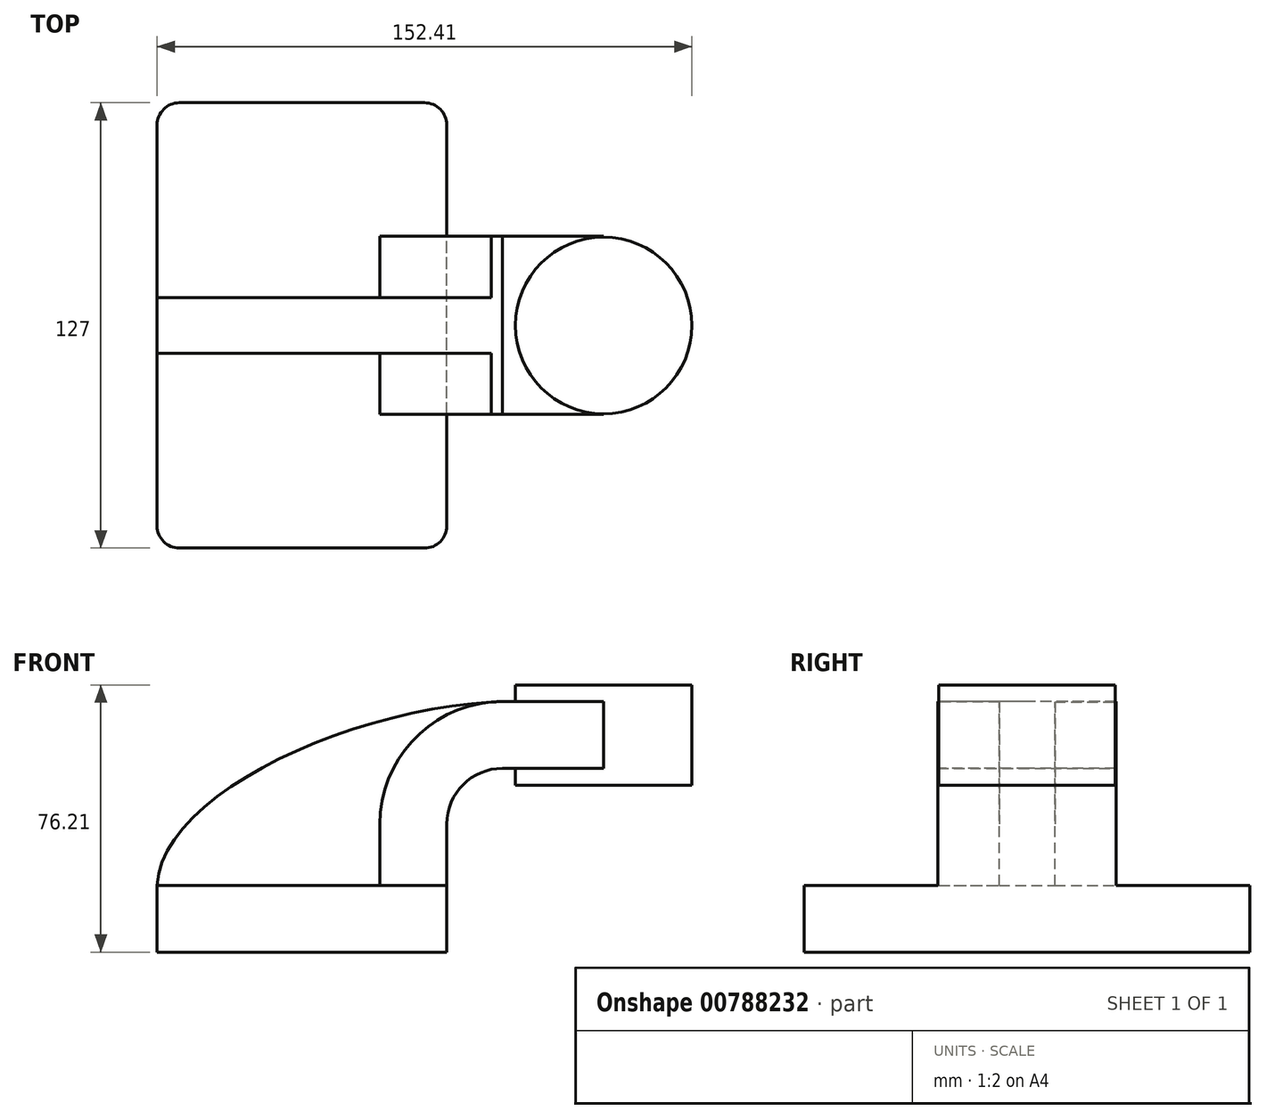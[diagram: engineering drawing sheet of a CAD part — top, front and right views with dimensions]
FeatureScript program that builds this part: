
annotation { "Feature Type Name" : "Feature", "Feature Type Description" : "" }
export const myFeature = defineFeature(function(context is Context, id is Id, definition is map)
    precondition{}
    {
        {
            var Q0;
            Q0=qCreatedBy(makeId("Front.planeOp"),FACE);
            var sketch = newSketch(context, id + "F0", { "sketchPlane" : qUnion([Q0])});
            skLineSegment(sketch, "E0.bottom", {"start": v(-41.27, -9.53) * mm, "end": v(41.28, -9.53) * mm});
            skLineSegment(sketch, "E0.top", {"start": v(-41.28, 9.53) * mm, "end": v(41.28, 9.53) * mm});
            skLineSegment(sketch, "E0.left", {"start": v(-41.28, -9.53) * mm, "end": v(-41.28, 9.53) * mm});
            skLineSegment(sketch, "E0.right", {"start": v(41.28, -9.53) * mm, "end": v(41.28, 9.53) * mm});
            skPoint(sketch, "E0.middle", {"position": v(0, 0) * mm});
            skLineSegment(sketch, "E1.bottom", {"start": v(60.32, 38.1) * mm, "end": v(111.12, 38.1) * mm});
            skLineSegment(sketch, "E1.top", {"start": v(60.32, 66.67) * mm, "end": v(111.12, 66.67) * mm});
            skLineSegment(sketch, "E1.left", {"start": v(60.32, 38.1) * mm, "end": v(60.32, 66.67) * mm});
            skLineSegment(sketch, "E1.right", {"start": v(111.12, 38.1) * mm, "end": v(111.12, 66.67) * mm});
            skPoint(sketch, "E1.middle", {"position": v(85.72, 52.39) * mm});
            skLineSegment(sketch, "E2", {"start": v(41.27, 9.53) * mm, "end": v(41.27, 27) * mm});
            skArc(sketch, "E3", {"start": v(41.27, 27) * mm, "mid": v(45.92, 38.23) * mm, "end": v(57.15, 42.88) * mm});
            skLineSegment(sketch, "E4", {"start": v(57.15, 42.88) * mm, "end": v(85.96, 42.88) * mm});
            skLineSegment(sketch, "E5.0", {"start": v(57.15, 61.93) * mm, "end": v(85.96, 61.93) * mm});
            skArc(sketch, "E5.1", {"start": v(22.23, 27) * mm, "mid": v(32.45, 51.7) * mm, "end": v(57.15, 61.93) * mm});
            skLineSegment(sketch, "E5.2", {"start": v(22.22, 9.53) * mm, "end": v(22.22, 27) * mm});
            skLineSegment(sketch, "E6", {"start": v(85.96, 38.1) * mm, "end": v(85.96, 66.68) * mm});
            skFitSpline(sketch, "E7", {"points": [v(-41.27, 9.53) * mm, v(57.15, 61.93) * mm], "startDerivative": vector(3.58, 78.44) * mm, "endDerivative": vector(127.7, 4.21) * mm});
            skSolve(sketch);
        }
        {
            var Q0;
            Q0=makeQuery(id+"F0.imprint","IMPRINT",FACE,{"disambiguationData":[TD([[makeQuery(id+"F0.imprint","IMPRINT",EDGE,{"derivedFrom":sQuery(id+"F0.wireOp",EDGE,"E0.bottom")}),1.0]])]});
            extrude(context, id + "F1", {"entities" : qUnion([Q0]), "endBound" : BoundingType.SYMMETRIC, "depth" : 127 * mm, "offsetDistance" : 25.4 * mm});
        }
        {
            var Q0;
            {var subQ0=sQuery(id+"F0.wireOp",EDGE,"E4");var subQ1=sQuery(id+"F0.wireOp",EDGE,"E1.left");var subQ2=makeQuery(id+"F0.imprint","INTERSECT",VERTEX,{"derivedFrom":[subQ1,subQ0]});Q0=makeQuery(id+"F0.imprint","IMPRINT",FACE,{"disambiguationData":[TD([[makeQuery(id+"F0.imprint","IMPRINT",EDGE,{"disambiguationData":[TD([[subQ2,-1.0]])],"derivedFrom":subQ1}),-1.0]])]});}
            var Q1;
            {var subQ1=sQuery(id+"F0.wireOp",EDGE,"E2");Q1=makeQuery(id+"F0.imprint","IMPRINT",FACE,{"disambiguationData":[TD([[makeQuery(id+"F0.imprint","IMPRINT",EDGE,{"derivedFrom":subQ1}),1.0]])]});}
            extrude(context, id + "F2", {"entities" : qUnion([Q0, Q1]), "operationType" : NewBodyOperationType.ADD, "endBound" : BoundingType.SYMMETRIC, "depth" : 50.8 * mm, "offsetDistance" : 25.4 * mm});
        }
        {
            var Q0;
            {var subQ3=sQuery(id+"F0.wireOp",EDGE,"E5.2");Q0=makeQuery(id+"F0.imprint","IMPRINT",FACE,{"disambiguationData":[TD([[makeQuery(id+"F0.imprint","IMPRINT",EDGE,{"derivedFrom":subQ3}),1.0]])]});}
            extrude(context, id + "F3", {"entities" : qUnion([Q0]), "operationType" : NewBodyOperationType.ADD, "endBound" : BoundingType.SYMMETRIC, "depth" : 15.88 * mm, "offsetDistance" : 25.4 * mm});
        }
        {
            var Q0;
            {var subQ4=sQuery(id+"F0.wireOp",EDGE,"E1.right");Q0=makeQuery(id+"F0.imprint","IMPRINT",FACE,{"disambiguationData":[TD([[makeQuery(id+"F0.imprint","IMPRINT",EDGE,{"derivedFrom":subQ4}),1.0]])]});}
            var Q1;
            Q1=sQuery(id+"F0.wireOp",EDGE,"E6");
            revolve(context, id + "F4", {"operationType" : NewBodyOperationType.ADD, "surfaceOperationType" : NewSurfaceOperationType.NEW, "entities" : qUnion([Q0]), "axis" : qUnion([Q1]), "revolveType" : RevolveType.FULL});
        }
        {
            var Q0;
            Q0=makeQuery(id+"F1.opExtrude","CAP_EDGE",EDGE,{"disambiguationData":[OSD([sQuery(id+"F0.wireOp",EDGE,"E0.right")])],"isStart":false});
            var Q1;
            Q1=makeQuery(id+"F1.opExtrude","CAP_EDGE",EDGE,{"disambiguationData":[OSD([sQuery(id+"F0.wireOp",EDGE,"E0.left")])],"isStart":false});
            var Q2;
            Q2=makeQuery(id+"F1.opExtrude","CAP_EDGE",EDGE,{"disambiguationData":[OSD([sQuery(id+"F0.wireOp",EDGE,"E0.left")])],"isStart":true});
            var Q3;
            Q3=makeQuery(id+"F1.opExtrude","CAP_EDGE",EDGE,{"disambiguationData":[OSD([sQuery(id+"F0.wireOp",EDGE,"E0.right")])],"isStart":true});
            fillet(context, id + "F5", {"entities" : qUnion([Q0, Q1, Q2, Q3]), "radius" : 6.35 * mm, "tangentPropagation" : true, "allowEdgeOverflow" : false});
        }
    });
